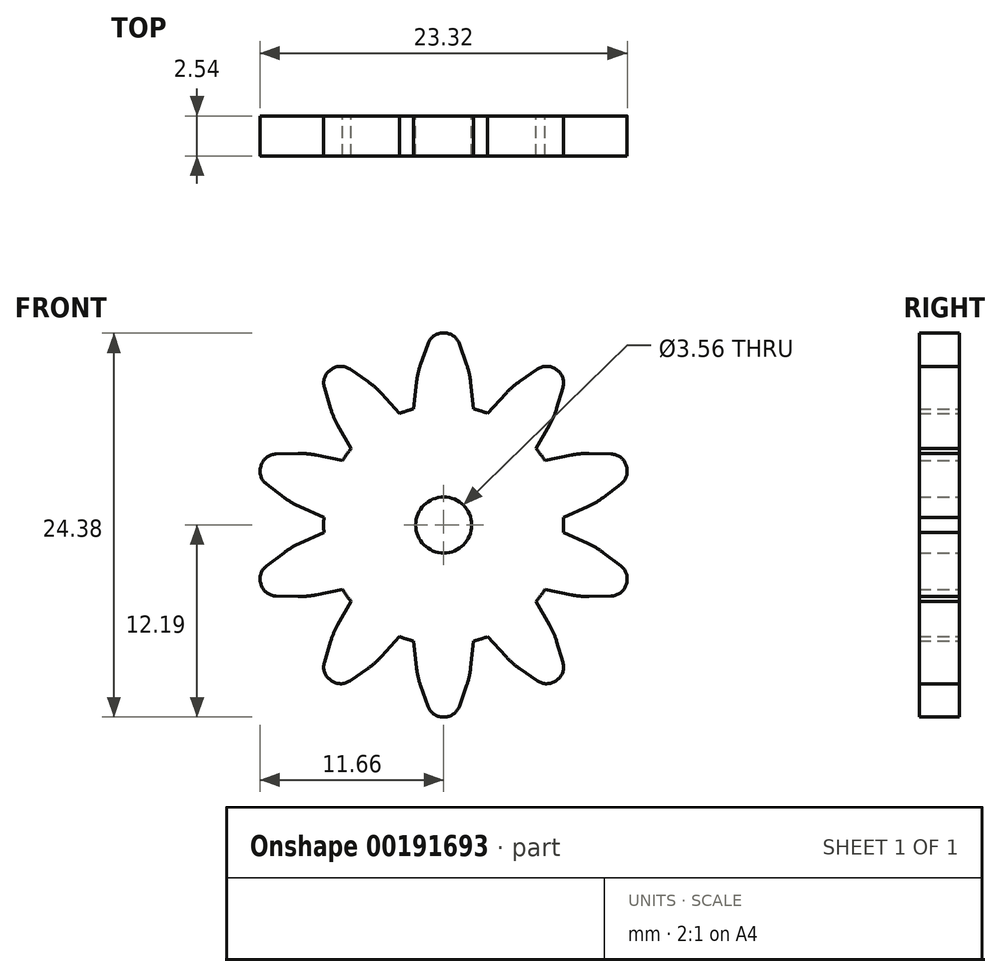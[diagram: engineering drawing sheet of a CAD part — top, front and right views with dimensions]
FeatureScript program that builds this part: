
annotation { "Feature Type Name" : "Feature", "Feature Type Description" : "" }
export const myFeature = defineFeature(function(context is Context, id is Id, definition is map)
    precondition{}
    {
        {
            var Q0;
            Q0=qCreatedBy(makeId("Front.planeOp"),FACE);
            var sketch = newSketch(context, id + "F0", { "sketchPlane" : qUnion([Q0])});
            skCircle(sketch, "E0", {"center": v(0, 0) * mm, "radius": 7.62 * mm});
            skLineSegment(sketch, "E1", {"start": v(-1.9, 7.38) * mm, "end": v(-0.76, 12.2) * mm, "construction": true});
            skLineSegment(sketch, "E2", {"start": v(-0.76, 12.2) * mm, "end": v(0.76, 12.2) * mm});
            skLineSegment(sketch, "E3", {"start": v(0.76, 12.2) * mm, "end": v(1.9, 7.38) * mm, "construction": true});
            skLineSegment(sketch, "E4", {"start": v(-1.9, 7.38) * mm, "end": v(-1.65, 9.65) * mm});
            skPoint(sketch, "E4.endSnap0", {"position": v(-1.33, 9.79) * mm});
            skLineSegment(sketch, "E5", {"start": v(-1.65, 9.65) * mm, "end": v(-0.76, 12.2) * mm});
            skLineSegment(sketch, "E6", {"start": v(1.9, 7.38) * mm, "end": v(1.65, 9.65) * mm});
            skPoint(sketch, "E6.endSnap0", {"position": v(1.33, 9.79) * mm});
            skLineSegment(sketch, "E7", {"start": v(1.65, 9.65) * mm, "end": v(0.76, 12.2) * mm});
            skLineSegment(sketch, "E8.1.0", {"start": v(-7.78, 9.42) * mm, "end": v(-6.55, 10.31) * mm});
            skLineSegment(sketch, "E8.1.1", {"start": v(-4.34, 8.78) * mm, "end": v(-6.55, 10.31) * mm});
            skLineSegment(sketch, "E8.1.2", {"start": v(-2.8, 7.09) * mm, "end": v(-4.34, 8.78) * mm});
            skLineSegment(sketch, "E8.1.3", {"start": v(-7, 6.84) * mm, "end": v(-7.78, 9.42) * mm});
            skLineSegment(sketch, "E8.1.4", {"start": v(-5.88, 4.85) * mm, "end": v(-7, 6.84) * mm});
            skLineSegment(sketch, "E8.2.0", {"start": v(-11.83, 3.04) * mm, "end": v(-11.36, 4.5) * mm});
            skLineSegment(sketch, "E8.2.1", {"start": v(-8.67, 4.55) * mm, "end": v(-11.36, 4.5) * mm});
            skLineSegment(sketch, "E8.2.2", {"start": v(-6.43, 4.1) * mm, "end": v(-8.67, 4.55) * mm});
            skLineSegment(sketch, "E8.2.3", {"start": v(-9.69, 1.41) * mm, "end": v(-11.83, 3.04) * mm});
            skLineSegment(sketch, "E8.2.4", {"start": v(-7.6, 0.47) * mm, "end": v(-9.69, 1.41) * mm});
            skLineSegment(sketch, "E8.3.0", {"start": v(-11.36, -4.5) * mm, "end": v(-11.83, -3.04) * mm});
            skLineSegment(sketch, "E8.3.1", {"start": v(-9.69, -1.41) * mm, "end": v(-11.83, -3.04) * mm});
            skLineSegment(sketch, "E8.3.2", {"start": v(-7.6, -0.47) * mm, "end": v(-9.69, -1.41) * mm});
            skLineSegment(sketch, "E8.3.3", {"start": v(-8.67, -4.55) * mm, "end": v(-11.36, -4.5) * mm});
            skLineSegment(sketch, "E8.3.4", {"start": v(-6.43, -4.1) * mm, "end": v(-8.67, -4.55) * mm});
            skLineSegment(sketch, "E8.4.0", {"start": v(-6.55, -10.31) * mm, "end": v(-7.78, -9.42) * mm});
            skLineSegment(sketch, "E8.4.1", {"start": v(-7, -6.84) * mm, "end": v(-7.78, -9.42) * mm});
            skLineSegment(sketch, "E8.4.2", {"start": v(-5.88, -4.85) * mm, "end": v(-7, -6.84) * mm});
            skLineSegment(sketch, "E8.4.3", {"start": v(-4.34, -8.78) * mm, "end": v(-6.55, -10.31) * mm});
            skLineSegment(sketch, "E8.4.4", {"start": v(-2.8, -7.09) * mm, "end": v(-4.34, -8.78) * mm});
            skLineSegment(sketch, "E8.5.0", {"start": v(0.76, -12.2) * mm, "end": v(-0.76, -12.2) * mm});
            skLineSegment(sketch, "E8.5.1", {"start": v(-1.65, -9.65) * mm, "end": v(-0.76, -12.2) * mm});
            skLineSegment(sketch, "E8.5.2", {"start": v(-1.9, -7.38) * mm, "end": v(-1.65, -9.65) * mm});
            skLineSegment(sketch, "E8.5.3", {"start": v(1.65, -9.65) * mm, "end": v(0.76, -12.2) * mm});
            skLineSegment(sketch, "E8.5.4", {"start": v(1.9, -7.38) * mm, "end": v(1.65, -9.65) * mm});
            skLineSegment(sketch, "E8.6.0", {"start": v(7.78, -9.42) * mm, "end": v(6.55, -10.31) * mm});
            skLineSegment(sketch, "E8.6.1", {"start": v(4.34, -8.78) * mm, "end": v(6.55, -10.31) * mm});
            skLineSegment(sketch, "E8.6.2", {"start": v(2.8, -7.09) * mm, "end": v(4.34, -8.78) * mm});
            skLineSegment(sketch, "E8.6.3", {"start": v(7, -6.84) * mm, "end": v(7.78, -9.42) * mm});
            skLineSegment(sketch, "E8.6.4", {"start": v(5.88, -4.85) * mm, "end": v(7, -6.84) * mm});
            skLineSegment(sketch, "E8.7.0", {"start": v(11.83, -3.04) * mm, "end": v(11.36, -4.5) * mm});
            skLineSegment(sketch, "E8.7.1", {"start": v(8.67, -4.55) * mm, "end": v(11.36, -4.5) * mm});
            skLineSegment(sketch, "E8.7.2", {"start": v(6.43, -4.1) * mm, "end": v(8.67, -4.55) * mm});
            skLineSegment(sketch, "E8.7.3", {"start": v(9.69, -1.41) * mm, "end": v(11.83, -3.04) * mm});
            skLineSegment(sketch, "E8.7.4", {"start": v(7.6, -0.47) * mm, "end": v(9.69, -1.41) * mm});
            skLineSegment(sketch, "E8.8.0", {"start": v(11.36, 4.5) * mm, "end": v(11.83, 3.04) * mm});
            skLineSegment(sketch, "E8.8.1", {"start": v(9.69, 1.41) * mm, "end": v(11.83, 3.04) * mm});
            skLineSegment(sketch, "E8.8.2", {"start": v(7.6, 0.47) * mm, "end": v(9.69, 1.41) * mm});
            skLineSegment(sketch, "E8.8.3", {"start": v(8.67, 4.55) * mm, "end": v(11.36, 4.5) * mm});
            skLineSegment(sketch, "E8.8.4", {"start": v(6.43, 4.1) * mm, "end": v(8.67, 4.55) * mm});
            skLineSegment(sketch, "E8.9.0", {"start": v(6.55, 10.31) * mm, "end": v(7.78, 9.42) * mm});
            skLineSegment(sketch, "E8.9.1", {"start": v(7, 6.84) * mm, "end": v(7.78, 9.42) * mm});
            skLineSegment(sketch, "E8.9.2", {"start": v(5.88, 4.85) * mm, "end": v(7, 6.84) * mm});
            skLineSegment(sketch, "E8.9.3", {"start": v(4.34, 8.78) * mm, "end": v(6.55, 10.31) * mm});
            skLineSegment(sketch, "E8.9.4", {"start": v(2.8, 7.09) * mm, "end": v(4.34, 8.78) * mm});
            skCircle(sketch, "E9", {"center": v(0, 0) * mm, "radius": 1.78 * mm});
            skSolve(sketch);
        }
        {
            var Q0;
            Q0=qSketchRegion(id+"F0",true);
            extrude(context, id + "F1", {"entities" : qUnion([Q0]), "depth" : 2.54 * mm});
        }
        {
            var Q0;
            Q0=makeQuery(id+"F1.opExtrude","SWEPT_EDGE",EDGE,{"disambiguationData":[OSD([sQuery(id+"F0.wireOp",EDGE,"E8.9.1"),sQuery(id+"F0.wireOp",EDGE,"E8.9.2")])]});
            var Q1;
            Q1=makeQuery(id+"F1.opExtrude","SWEPT_EDGE",EDGE,{"disambiguationData":[OSD([sQuery(id+"F0.wireOp",EDGE,"E8.9.3"),sQuery(id+"F0.wireOp",EDGE,"E8.9.4")])]});
            var Q2;
            Q2=makeQuery(id+"F1.opExtrude","SWEPT_EDGE",EDGE,{"disambiguationData":[OSD([sQuery(id+"F0.wireOp",EDGE,"E6"),sQuery(id+"F0.wireOp",EDGE,"E7")])]});
            var Q3;
            Q3=makeQuery(id+"F1.opExtrude","SWEPT_EDGE",EDGE,{"disambiguationData":[OSD([sQuery(id+"F0.wireOp",EDGE,"E8.1.1"),sQuery(id+"F0.wireOp",EDGE,"E8.1.2")])]});
            var Q4;
            Q4=makeQuery(id+"F1.opExtrude","SWEPT_EDGE",EDGE,{"disambiguationData":[OSD([sQuery(id+"F0.wireOp",EDGE,"E8.2.1"),sQuery(id+"F0.wireOp",EDGE,"E8.2.2")])]});
            var Q5;
            Q5=makeQuery(id+"F1.opExtrude","SWEPT_EDGE",EDGE,{"disambiguationData":[OSD([sQuery(id+"F0.wireOp",EDGE,"E8.3.1"),sQuery(id+"F0.wireOp",EDGE,"E8.3.2")])]});
            var Q6;
            Q6=makeQuery(id+"F1.opExtrude","SWEPT_EDGE",EDGE,{"disambiguationData":[OSD([sQuery(id+"F0.wireOp",EDGE,"E8.4.1"),sQuery(id+"F0.wireOp",EDGE,"E8.4.2")])]});
            var Q7;
            Q7=makeQuery(id+"F1.opExtrude","SWEPT_EDGE",EDGE,{"disambiguationData":[OSD([sQuery(id+"F0.wireOp",EDGE,"E8.5.1"),sQuery(id+"F0.wireOp",EDGE,"E8.5.2")])]});
            var Q8;
            Q8=makeQuery(id+"F1.opExtrude","SWEPT_EDGE",EDGE,{"disambiguationData":[OSD([sQuery(id+"F0.wireOp",EDGE,"E8.6.1"),sQuery(id+"F0.wireOp",EDGE,"E8.6.2")])]});
            var Q9;
            Q9=makeQuery(id+"F1.opExtrude","SWEPT_EDGE",EDGE,{"disambiguationData":[OSD([sQuery(id+"F0.wireOp",EDGE,"E8.7.1"),sQuery(id+"F0.wireOp",EDGE,"E8.7.2")])]});
            var Q10;
            Q10=makeQuery(id+"F1.opExtrude","SWEPT_EDGE",EDGE,{"disambiguationData":[OSD([sQuery(id+"F0.wireOp",EDGE,"E8.8.1"),sQuery(id+"F0.wireOp",EDGE,"E8.8.2")])]});
            var Q11;
            Q11=makeQuery(id+"F1.opExtrude","SWEPT_EDGE",EDGE,{"disambiguationData":[OSD([sQuery(id+"F0.wireOp",EDGE,"E8.7.3"),sQuery(id+"F0.wireOp",EDGE,"E8.7.4")])]});
            var Q12;
            Q12=makeQuery(id+"F1.opExtrude","SWEPT_EDGE",EDGE,{"disambiguationData":[OSD([sQuery(id+"F0.wireOp",EDGE,"E8.8.3"),sQuery(id+"F0.wireOp",EDGE,"E8.8.4")])]});
            var Q13;
            Q13=makeQuery(id+"F1.opExtrude","SWEPT_EDGE",EDGE,{"disambiguationData":[OSD([sQuery(id+"F0.wireOp",EDGE,"E4"),sQuery(id+"F0.wireOp",EDGE,"E5")])]});
            var Q14;
            Q14=makeQuery(id+"F1.opExtrude","SWEPT_EDGE",EDGE,{"disambiguationData":[OSD([sQuery(id+"F0.wireOp",EDGE,"E8.1.3"),sQuery(id+"F0.wireOp",EDGE,"E8.1.4")])]});
            var Q15;
            Q15=makeQuery(id+"F1.opExtrude","SWEPT_EDGE",EDGE,{"disambiguationData":[OSD([sQuery(id+"F0.wireOp",EDGE,"E8.2.3"),sQuery(id+"F0.wireOp",EDGE,"E8.2.4")])]});
            var Q16;
            Q16=makeQuery(id+"F1.opExtrude","SWEPT_EDGE",EDGE,{"disambiguationData":[OSD([sQuery(id+"F0.wireOp",EDGE,"E8.3.3"),sQuery(id+"F0.wireOp",EDGE,"E8.3.4")])]});
            var Q17;
            Q17=makeQuery(id+"F1.opExtrude","SWEPT_EDGE",EDGE,{"disambiguationData":[OSD([sQuery(id+"F0.wireOp",EDGE,"E8.4.3"),sQuery(id+"F0.wireOp",EDGE,"E8.4.4")])]});
            var Q18;
            Q18=makeQuery(id+"F1.opExtrude","SWEPT_EDGE",EDGE,{"disambiguationData":[OSD([sQuery(id+"F0.wireOp",EDGE,"E8.5.3"),sQuery(id+"F0.wireOp",EDGE,"E8.5.4")])]});
            var Q19;
            Q19=makeQuery(id+"F1.opExtrude","SWEPT_EDGE",EDGE,{"disambiguationData":[OSD([sQuery(id+"F0.wireOp",EDGE,"E8.6.3"),sQuery(id+"F0.wireOp",EDGE,"E8.6.4")])]});
            fillet(context, id + "F2", {"entities" : qUnion([Q0, Q1, Q2, Q3, Q4, Q5, Q6, Q7, Q8, Q9, Q10, Q11, Q12, Q13, Q14, Q15, Q16, Q17, Q18, Q19]), "radius" : 5.08 * mm, "tangentPropagation" : true, "allowEdgeOverflow" : false});
        }
        {
            var Q0;
            Q0=makeQuery(id+"F1.opExtrude","SWEPT_EDGE",EDGE,{"disambiguationData":[OSD([sQuery(id+"F0.wireOp",EDGE,"E2"),sQuery(id+"F0.wireOp",EDGE,"E7")])]});
            var Q1;
            Q1=makeQuery(id+"F1.opExtrude","SWEPT_EDGE",EDGE,{"disambiguationData":[OSD([sQuery(id+"F0.wireOp",EDGE,"E2"),sQuery(id+"F0.wireOp",EDGE,"E5")])]});
            var Q2;
            Q2=makeQuery(id+"F1.opExtrude","SWEPT_EDGE",EDGE,{"disambiguationData":[OSD([sQuery(id+"F0.wireOp",EDGE,"E8.1.0"),sQuery(id+"F0.wireOp",EDGE,"E8.1.1")])]});
            var Q3;
            Q3=makeQuery(id+"F1.opExtrude","SWEPT_EDGE",EDGE,{"disambiguationData":[OSD([sQuery(id+"F0.wireOp",EDGE,"E8.1.0"),sQuery(id+"F0.wireOp",EDGE,"E8.1.3")])]});
            var Q4;
            Q4=makeQuery(id+"F1.opExtrude","SWEPT_EDGE",EDGE,{"disambiguationData":[OSD([sQuery(id+"F0.wireOp",EDGE,"E8.2.0"),sQuery(id+"F0.wireOp",EDGE,"E8.2.1")])]});
            var Q5;
            Q5=makeQuery(id+"F1.opExtrude","SWEPT_EDGE",EDGE,{"disambiguationData":[OSD([sQuery(id+"F0.wireOp",EDGE,"E8.9.0"),sQuery(id+"F0.wireOp",EDGE,"E8.9.3")])]});
            var Q6;
            Q6=makeQuery(id+"F1.opExtrude","SWEPT_EDGE",EDGE,{"disambiguationData":[OSD([sQuery(id+"F0.wireOp",EDGE,"E8.9.0"),sQuery(id+"F0.wireOp",EDGE,"E8.9.1")])]});
            var Q7;
            Q7=makeQuery(id+"F1.opExtrude","SWEPT_EDGE",EDGE,{"disambiguationData":[OSD([sQuery(id+"F0.wireOp",EDGE,"E8.8.0"),sQuery(id+"F0.wireOp",EDGE,"E8.8.3")])]});
            var Q8;
            Q8=makeQuery(id+"F1.opExtrude","SWEPT_EDGE",EDGE,{"disambiguationData":[OSD([sQuery(id+"F0.wireOp",EDGE,"E8.2.0"),sQuery(id+"F0.wireOp",EDGE,"E8.2.3")])]});
            var Q9;
            Q9=makeQuery(id+"F1.opExtrude","SWEPT_EDGE",EDGE,{"disambiguationData":[OSD([sQuery(id+"F0.wireOp",EDGE,"E8.3.0"),sQuery(id+"F0.wireOp",EDGE,"E8.3.1")])]});
            var Q10;
            Q10=makeQuery(id+"F1.opExtrude","SWEPT_EDGE",EDGE,{"disambiguationData":[OSD([sQuery(id+"F0.wireOp",EDGE,"E8.3.0"),sQuery(id+"F0.wireOp",EDGE,"E8.3.3")])]});
            var Q11;
            Q11=makeQuery(id+"F1.opExtrude","SWEPT_EDGE",EDGE,{"disambiguationData":[OSD([sQuery(id+"F0.wireOp",EDGE,"E8.4.0"),sQuery(id+"F0.wireOp",EDGE,"E8.4.1")])]});
            var Q12;
            Q12=makeQuery(id+"F1.opExtrude","SWEPT_EDGE",EDGE,{"disambiguationData":[OSD([sQuery(id+"F0.wireOp",EDGE,"E8.4.0"),sQuery(id+"F0.wireOp",EDGE,"E8.4.3")])]});
            var Q13;
            Q13=makeQuery(id+"F1.opExtrude","SWEPT_EDGE",EDGE,{"disambiguationData":[OSD([sQuery(id+"F0.wireOp",EDGE,"E8.5.0"),sQuery(id+"F0.wireOp",EDGE,"E8.5.1")])]});
            var Q14;
            Q14=makeQuery(id+"F1.opExtrude","SWEPT_EDGE",EDGE,{"disambiguationData":[OSD([sQuery(id+"F0.wireOp",EDGE,"E8.5.0"),sQuery(id+"F0.wireOp",EDGE,"E8.5.3")])]});
            var Q15;
            Q15=makeQuery(id+"F1.opExtrude","SWEPT_EDGE",EDGE,{"disambiguationData":[OSD([sQuery(id+"F0.wireOp",EDGE,"E8.6.0"),sQuery(id+"F0.wireOp",EDGE,"E8.6.1")])]});
            var Q16;
            Q16=makeQuery(id+"F1.opExtrude","SWEPT_EDGE",EDGE,{"disambiguationData":[OSD([sQuery(id+"F0.wireOp",EDGE,"E8.6.0"),sQuery(id+"F0.wireOp",EDGE,"E8.6.3")])]});
            var Q17;
            Q17=makeQuery(id+"F1.opExtrude","SWEPT_EDGE",EDGE,{"disambiguationData":[OSD([sQuery(id+"F0.wireOp",EDGE,"E8.7.0"),sQuery(id+"F0.wireOp",EDGE,"E8.7.3")])]});
            var Q18;
            Q18=makeQuery(id+"F1.opExtrude","SWEPT_EDGE",EDGE,{"disambiguationData":[OSD([sQuery(id+"F0.wireOp",EDGE,"E8.7.0"),sQuery(id+"F0.wireOp",EDGE,"E8.7.1")])]});
            var Q19;
            Q19=makeQuery(id+"F1.opExtrude","SWEPT_EDGE",EDGE,{"disambiguationData":[OSD([sQuery(id+"F0.wireOp",EDGE,"E8.8.0"),sQuery(id+"F0.wireOp",EDGE,"E8.8.1")])]});
            fillet(context, id + "F3", {"entities" : qUnion([Q0, Q1, Q2, Q3, Q4, Q5, Q6, Q7, Q8, Q9, Q10, Q11, Q12, Q13, Q14, Q15, Q16, Q17, Q18, Q19]), "radius" : 1.02 * mm, "tangentPropagation" : true, "allowEdgeOverflow" : false});
        }
    });
